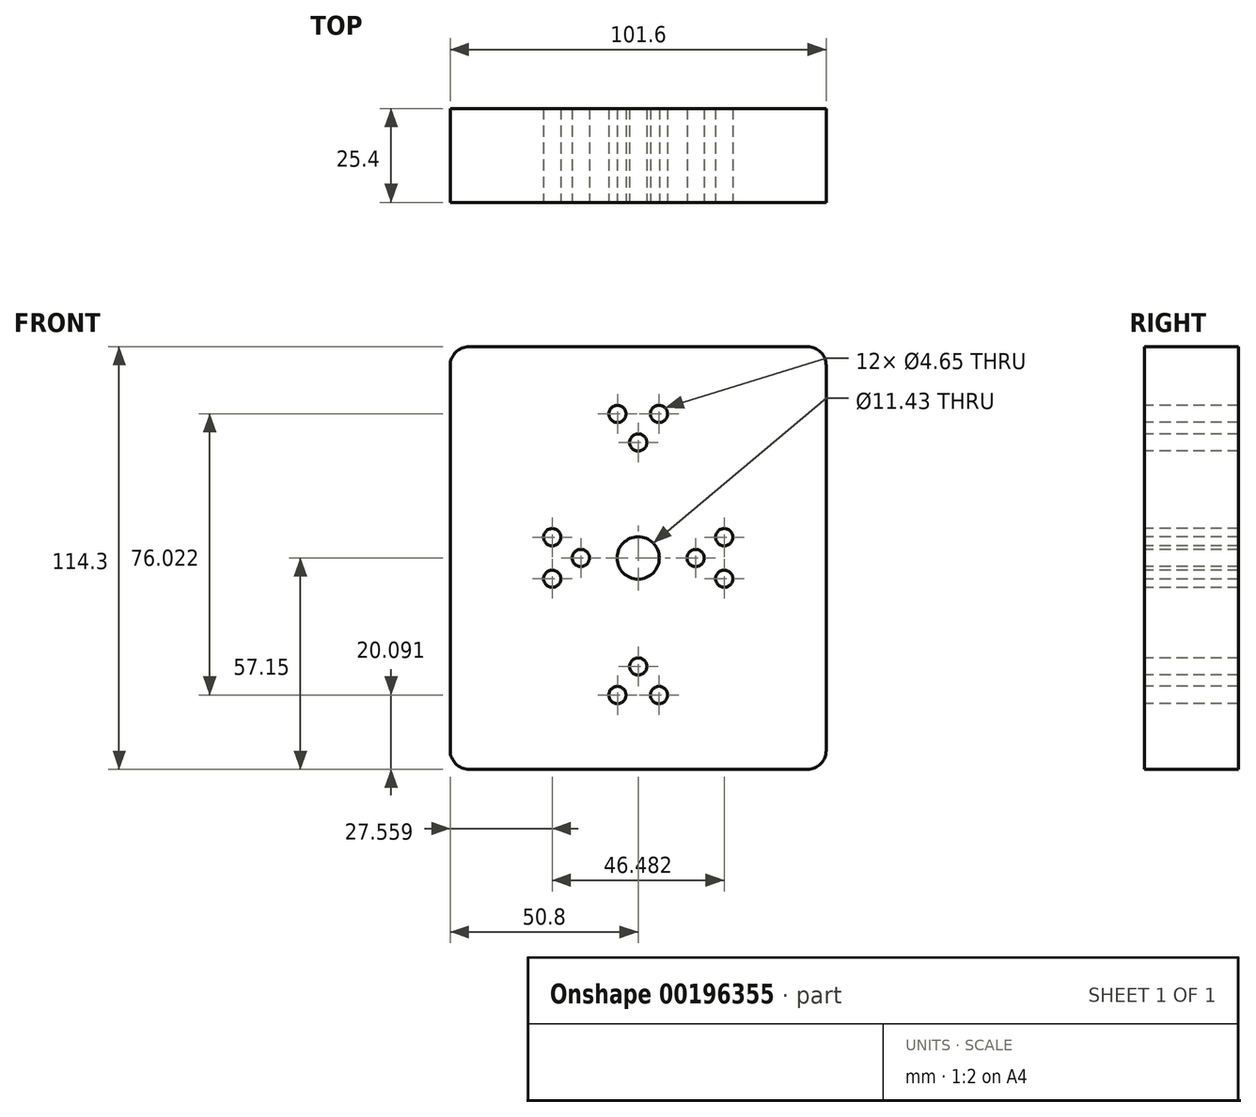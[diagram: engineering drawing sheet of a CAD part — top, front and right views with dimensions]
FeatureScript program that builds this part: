
annotation { "Feature Type Name" : "Feature", "Feature Type Description" : "" }
export const myFeature = defineFeature(function(context is Context, id is Id, definition is map)
    precondition{}
    {
        {
            var Q0;
            Q0=qCreatedBy(makeId("Front.planeOp"),FACE);
            var sketch = newSketch(context, id + "F0", { "sketchPlane" : qUnion([Q0])});
            skLineSegment(sketch, "E0.bottom", {"start": v(50.8, -57.15) * mm, "end": v(-50.8, -57.15) * mm});
            skLineSegment(sketch, "E0.top", {"start": v(50.8, 57.15) * mm, "end": v(-50.8, 57.15) * mm});
            skLineSegment(sketch, "E0.left", {"start": v(50.8, -57.15) * mm, "end": v(50.8, 57.15) * mm});
            skLineSegment(sketch, "E0.right", {"start": v(-50.8, -57.15) * mm, "end": v(-50.8, 57.15) * mm});
            skPoint(sketch, "E0.middle", {"position": v(0, 0) * mm});
            skSolve(sketch);
        }
        {
            var Q0;
            Q0 = qSketchRegion(id + "F0", true);
            extrude(context, id + "F1", {"entities" : qUnion([Q0]), "depth" : 25.4 * mm});
        }
        {
            var Q0;
            Q0=makeQuery(id+"F1.opExtrude","CAP_FACE",FACE,{"disambiguationData":[OSD([sQuery(id+"F0.wireOp",EDGE,"E0.bottom"),sQuery(id+"F0.wireOp",EDGE,"E0.top"),sQuery(id+"F0.wireOp",EDGE,"E0.left"),sQuery(id+"F0.wireOp",EDGE,"E0.right")])],"isStart":false});
            var sketch = newSketch(context, id + "F2", { "sketchPlane" : qUnion([Q0])});
            skCircle(sketch, "E1", {"center": v(0, 0) * mm, "radius": 5.72 * mm});
            skLineSegment(sketch, "E2", {"start": v(0, 5.72) * mm, "end": v(0, 28.9) * mm});
            skCircle(sketch, "E3", {"center": v(0, 31.23) * mm, "radius": 2.32 * mm});
            skLineSegment(sketch, "E4", {"start": v(0, 33.55) * mm, "end": v(0, 38.96) * mm});
            skLineSegment(sketch, "E5", {"start": v(0, 38.96) * mm, "end": v(3.29, 38.96) * mm});
            skLineSegment(sketch, "E6", {"start": v(0, 38.96) * mm, "end": v(-3.29, 38.96) * mm});
            skCircle(sketch, "E7", {"center": v(-5.61, 38.96) * mm, "radius": 2.32 * mm});
            skCircle(sketch, "E8", {"center": v(5.61, 38.96) * mm, "radius": 2.32 * mm});
            skCircle(sketch, "E9.MirrorC", {"center": v(0, -29.32) * mm, "radius": 2.32 * mm});
            skCircle(sketch, "E10.MirrorC", {"center": v(-5.61, -37.06) * mm, "radius": 2.32 * mm});
            skCircle(sketch, "E11.MirrorC", {"center": v(5.61, -37.06) * mm, "radius": 2.32 * mm});
            skPoint(sketch, "E12.trimOffspring.end.orphan", {"position": v(0, -57.15) * mm});
            skPoint(sketch, "E13.start.orphan", {"position": v(0, -5.72) * mm});
            skLineSegment(sketch, "E14", {"start": v(0, 57.15) * mm, "end": v(0, 28.9) * mm});
            skLineSegment(sketch, "E15", {"start": v(-5.72, 0) * mm, "end": v(-13.18, 0) * mm});
            skCircle(sketch, "E16", {"center": v(-15.5, 0) * mm, "radius": 2.32 * mm});
            skLineSegment(sketch, "E17", {"start": v(-17.83, 0) * mm, "end": v(-23.24, 0) * mm});
            skLineSegment(sketch, "E18", {"start": v(-23.24, 0) * mm, "end": v(-23.24, 3.3) * mm});
            skLineSegment(sketch, "E19", {"start": v(-23.24, 0) * mm, "end": v(-23.24, -3.3) * mm});
            skCircle(sketch, "E20", {"center": v(-23.24, 5.63) * mm, "radius": 2.32 * mm});
            skCircle(sketch, "E21", {"center": v(-23.24, -5.63) * mm, "radius": 2.32 * mm});
            skCircle(sketch, "E22.MirrorC", {"center": v(15.5, 0) * mm, "radius": 2.32 * mm});
            skCircle(sketch, "E23.MirrorC", {"center": v(23.24, -5.63) * mm, "radius": 2.32 * mm});
            skCircle(sketch, "E24.MirrorC", {"center": v(23.24, 5.63) * mm, "radius": 2.32 * mm});
            skLineSegment(sketch, "E25.trimOffspring", {"start": v(0, -5.72) * mm, "end": v(0, -57.15) * mm});
            skSolve(sketch);
        }
        {
            var Q0;
            Q0 = qSketchRegion(id + "F2", true);
            extrude(context, id + "F3", {"entities" : qUnion([Q0]), "operationType" : NewBodyOperationType.REMOVE, "endBound" : BoundingType.THROUGH_ALL, "oppositeDirection" : true, "depth" : 25.4 * mm});
        }
        {
            var Q0;
            Q0=makeQuery(id+"F1.opExtrude","SWEPT_EDGE",EDGE,{"disambiguationData":[OSD([sQuery(id+"F0.wireOp",EDGE,"E0.bottom"),sQuery(id+"F0.wireOp",EDGE,"E0.right")])]});
            var Q1;
            Q1=makeQuery(id+"F1.opExtrude","SWEPT_EDGE",EDGE,{"disambiguationData":[OSD([sQuery(id+"F0.wireOp",EDGE,"E0.bottom"),sQuery(id+"F0.wireOp",EDGE,"E0.left")])]});
            var Q2;
            Q2=makeQuery(id+"F1.opExtrude","SWEPT_EDGE",EDGE,{"disambiguationData":[OSD([sQuery(id+"F0.wireOp",EDGE,"E0.top"),sQuery(id+"F0.wireOp",EDGE,"E0.right")])]});
            var Q3;
            Q3=makeQuery(id+"F1.opExtrude","SWEPT_EDGE",EDGE,{"disambiguationData":[OSD([sQuery(id+"F0.wireOp",EDGE,"E0.top"),sQuery(id+"F0.wireOp",EDGE,"E0.left")])]});
            fillet(context, id + "F4", {"entities" : qUnion([Q0, Q1, Q2, Q3]), "radius" : 5.08 * mm, "tangentPropagation" : true, "allowEdgeOverflow" : false});
        }
    });
